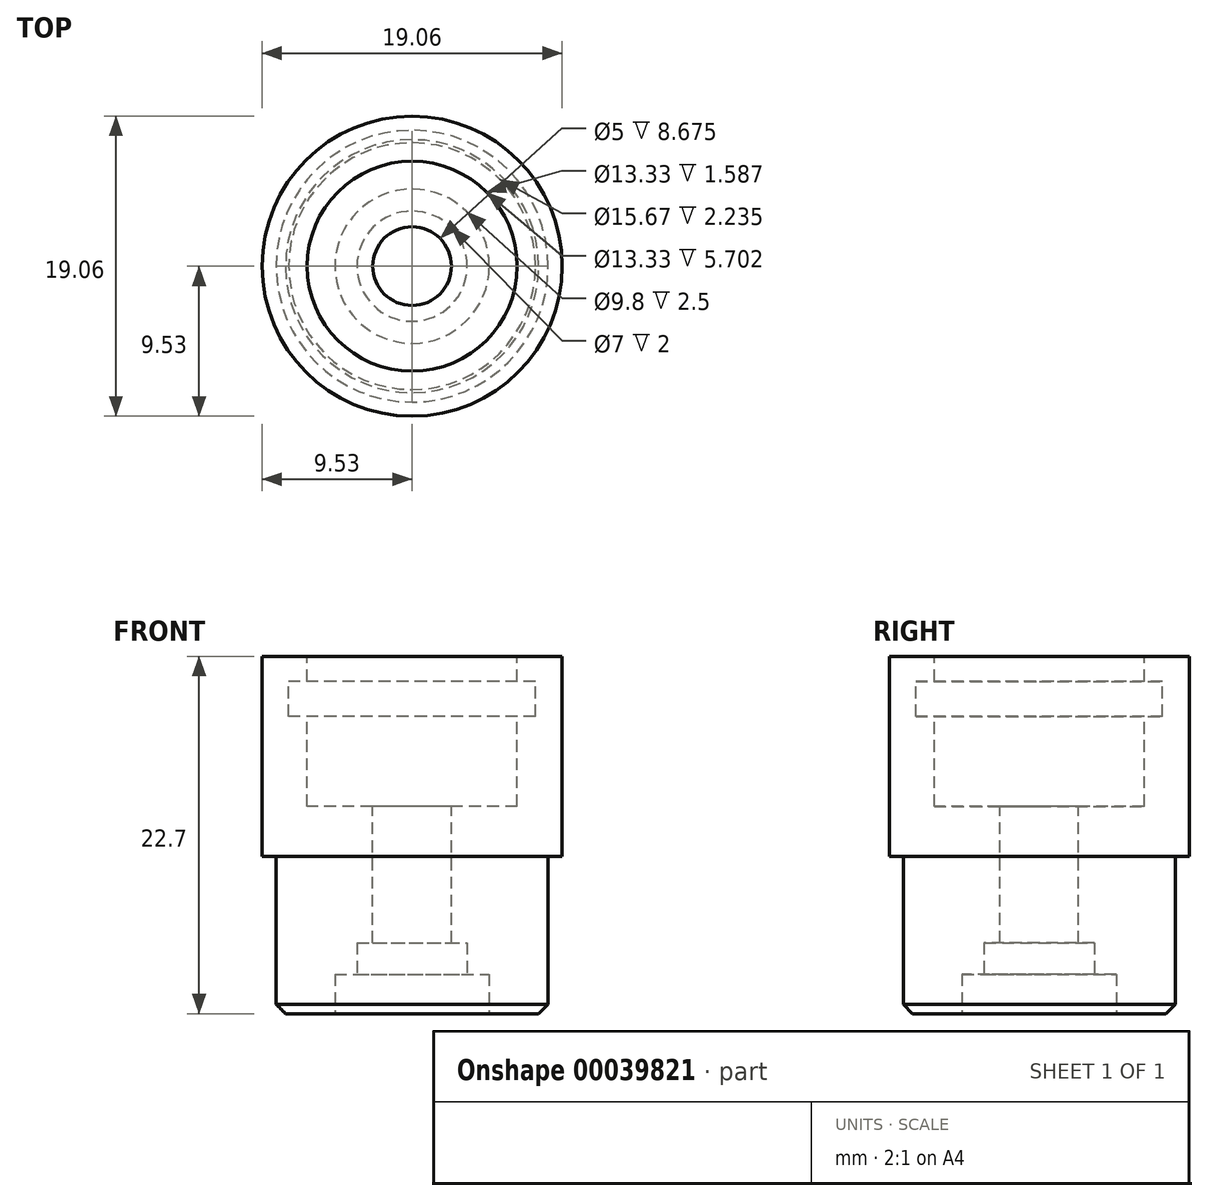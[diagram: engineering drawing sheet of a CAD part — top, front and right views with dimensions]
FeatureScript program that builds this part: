
annotation { "Feature Type Name" : "Feature", "Feature Type Description" : "" }
export const myFeature = defineFeature(function(context is Context, id is Id, definition is map)
    precondition{}
    {
        {
            var Q0;
            Q0=qCreatedBy(makeId("Top.planeOp"),FACE);
            var sketch = newSketch(context, id + "F0", { "sketchPlane" : qUnion([Q0])});
            skCircle(sketch, "E0", {"center": v(0, 0) * mm, "radius": 9.53 * mm});
            skSolve(sketch);
        }
        {
            var Q0;
            Q0=qSketchRegion(id+"F0",true);
            extrude(context, id + "F1", {"entities" : qUnion([Q0]), "depth" : 12.7 * mm});
        }
        {
            var Q0;
            Q0=makeQuery(id+"F1.opExtrude","CAP_FACE",FACE,{"disambiguationData":[OSD([sQuery(id+"F0.wireOp",EDGE,"E0")])],"isStart":false});
            var sketch = newSketch(context, id + "F2", { "sketchPlane" : qUnion([Q0])});
            skCircle(sketch, "E1", {"center": v(0, 0) * mm, "radius": 6.67 * mm});
            skSolve(sketch);
        }
        {
            var Q0;
            Q0=qSketchRegion(id+"F2",true);
            extrude(context, id + "F3", {"entities" : qUnion([Q0]), "operationType" : NewBodyOperationType.REMOVE, "oppositeDirection" : true, "depth" : 9.52 * mm});
        }
        {
            var Q0;
            Q0=qCreatedBy(makeId("Front.planeOp"),FACE);
            var sketch = newSketch(context, id + "F4", { "sketchPlane" : qUnion([Q0])});
            skLineSegment(sketch, "E2.bottom", {"start": v(6.67, 11.11) * mm, "end": v(7.84, 11.11) * mm});
            skLineSegment(sketch, "E2.top", {"start": v(6.67, 8.88) * mm, "end": v(7.84, 8.88) * mm});
            skLineSegment(sketch, "E2.left", {"start": v(6.67, 11.11) * mm, "end": v(6.67, 8.88) * mm});
            skLineSegment(sketch, "E2.right", {"start": v(7.84, 11.11) * mm, "end": v(7.84, 8.88) * mm});
            skLineSegment(sketch, "E3", {"start": v(0, 0) * mm, "end": v(0, 38.04) * mm, "construction": true});
            skSolve(sketch);
        }
        {
            var Q0;
            Q0=qSketchRegion(id+"F4",true);
            var Q1;
            Q1=sQuery(id+"F4.wireOp",EDGE,"E3");
            revolve(context, id + "F5", {"operationType" : NewBodyOperationType.REMOVE, "entities" : qUnion([Q0]), "axis" : qUnion([Q1]), "revolveType" : RevolveType.FULL, "oppositeDirection" : true});
        }
        {
            var Q0;
            Q0=makeQuery(id+"F1.opExtrude","CAP_FACE",FACE,{"disambiguationData":[OSD([sQuery(id+"F0.wireOp",EDGE,"E0")])],"isStart":true});
            var sketch = newSketch(context, id + "F6", { "sketchPlane" : qUnion([Q0])});
            skCircle(sketch, "E4", {"center": v(0, 0) * mm, "radius": 8.64 * mm});
            skSolve(sketch);
        }
        {
            var Q0;
            Q0=qSketchRegion(id+"F6",true);
            extrude(context, id + "F7", {"entities" : qUnion([Q0]), "operationType" : NewBodyOperationType.ADD, "offsetDistance" : 25 * mm, "depth" : 10 * mm});
        }
        {
            var Q0;
            Q0=makeQuery(id+"F7.opExtrude","CAP_FACE",FACE,{"disambiguationData":[OSD([sQuery(id+"F6.wireOp",EDGE,"E4")])],"isStart":false});
            var sketch = newSketch(context, id + "F8", { "sketchPlane" : qUnion([Q0])});
            skCircle(sketch, "E5", {"center": v(0, 0) * mm, "radius": 4.9 * mm});
            skSolve(sketch);
        }
        {
            var Q0;
            Q0=qSketchRegion(id+"F8",true);
            var Q1;
            Q1=makeQuery(id+"F1.opExtrude","CAP_FACE",FACE,{"disambiguationData":[OSD([sQuery(id+"F0.wireOp",EDGE,"E0")])],"isStart":true});
            extrude(context, id + "F9", {"entities" : qUnion([Q0]), "operationType" : NewBodyOperationType.REMOVE, "oppositeDirection" : true, "endBoundEntityFace" : qUnion([Q1]), "offsetDistance" : 25 * mm, "depth" : 2.5 * mm});
        }
        {
            var Q0;
            Q0=makeQuery(id+"F3.boolean.opBoolean","COPY",FACE,{"derivedFrom":makeQuery(id+"F3.opExtrude","CAP_FACE",FACE,{"disambiguationData":[OSD([sQuery(id+"F2.wireOp",EDGE,"E1")])],"isStart":false})});
            var sketch = newSketch(context, id + "F10", { "sketchPlane" : qUnion([Q0])});
            skCircle(sketch, "E6", {"center": v(0, 0) * mm, "radius": 2.5 * mm});
            skSolve(sketch);
        }
        {
            var Q0;
            Q0=qSketchRegion(id+"F10",true);
            extrude(context, id + "F11", {"entities" : qUnion([Q0]), "operationType" : NewBodyOperationType.REMOVE, "oppositeDirection" : true, "depth" : 25.4 * mm});
        }
        {
            var Q0;
            Q0=makeQuery(id+"F9.boolean.opBoolean","COPY",FACE,{"derivedFrom":makeQuery(id+"F9.opExtrude","CAP_FACE",FACE,{"disambiguationData":[OSD([sQuery(id+"F8.wireOp",EDGE,"E5")])],"isStart":false})});
            var sketch = newSketch(context, id + "F12", { "sketchPlane" : qUnion([Q0])});
            skCircle(sketch, "E7", {"center": v(0, 0) * mm, "radius": 3.5 * mm});
            skSolve(sketch);
        }
        {
            var Q0;
            Q0 = qSketchRegion(id + "F12", true);
            extrude(context, id + "F13", {"entities" : qUnion([Q0]), "operationType" : NewBodyOperationType.REMOVE, "oppositeDirection" : true, "depth" : 2 * mm, "offsetDistance" : 25 * mm});
        }
        {
            var Q0;
            Q0=makeQuery(id+"F9.boolean.opBoolean","COPY",EDGE,{"derivedFrom":makeQuery(id+"F9.opExtrude","CAP_EDGE",EDGE,{"disambiguationData":[OSD([sQuery(id+"F8.wireOp",EDGE,"E5")])],"isStart":true})});
            var Q1;
            Q1=makeQuery(id+"F7.opExtrude","CAP_EDGE",EDGE,{"disambiguationData":[OSD([sQuery(id+"F6.wireOp",EDGE,"E4")])],"isStart":false});
            chamfer(context, id + "F14", {"entities" : qUnion([Q0, Q1]), "width" : .6 * mm, "tangentPropagation" : true});
        }
    });
